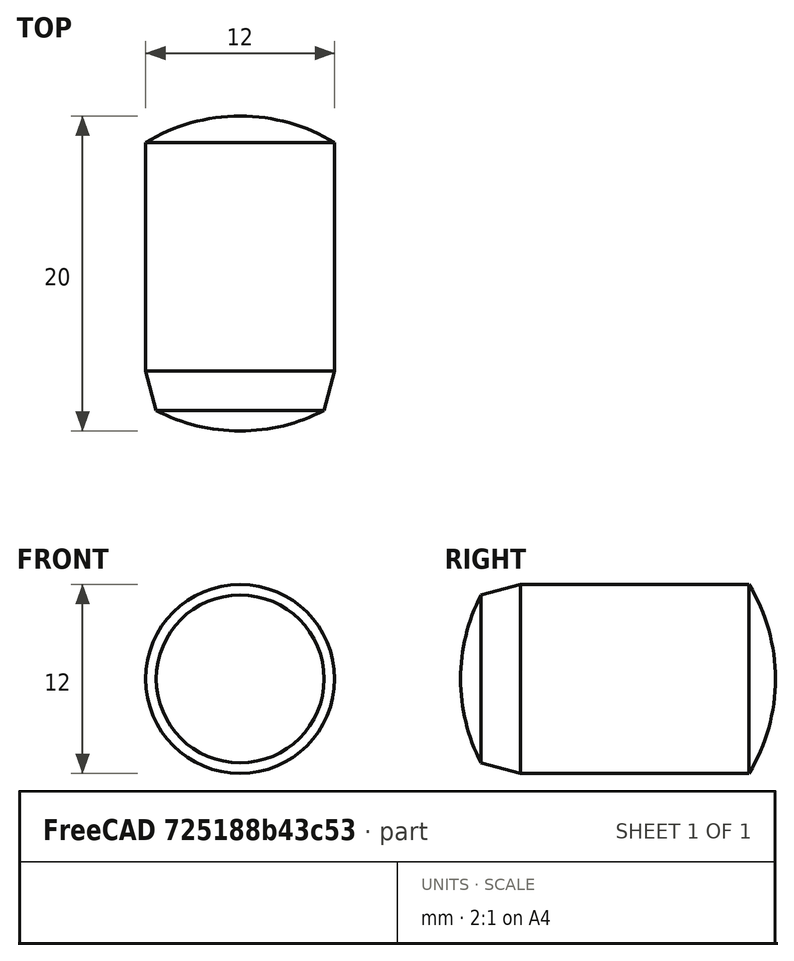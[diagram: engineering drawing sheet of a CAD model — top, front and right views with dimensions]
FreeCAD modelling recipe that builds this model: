
FCSTD DOCUMENT  (FreeCAD 0.15R4470 (Git))
Label: Zyl-Stift_DIN_6325-12x20
License: CC-BY 3.0
LicenseURL: http://creativecommons.org/licenses/by/3.0/
objects: Sketcher::SketchObject×1, PartDesign::Revolution×1
note: 3 computed .brp shape members not serialized (recipe doc carries the construction recipe); baked Part::Feature solids carry a one-line shape summary decoded from their .brp

FEATURE [Sketcher::SketchObject] Sketch
  Placement = pos=(0,0,0) rot=(0.57735,0.57735,0.57735;2.0944rad)
  sketch-geometry (5):
    g0: ArcOfCircle CenterX=10.277 CenterY=0 CenterZ=0 NormalX=0 NormalY=0 NormalZ=1 Radius=11.577 StartAngle=2.66314 EndAngle=3.14159
    g1: LineSegment StartX=0 StartY=5.33013 StartZ=0 EndX=2.5 EndY=6 EndZ=0
    g2: LineSegment StartX=2.5 StartY=6 StartZ=0 EndX=17.0239 EndY=6 EndZ=0
    g3: ArcOfCircle CenterX=7.12298 CenterY=0 CenterZ=0 NormalX=0 NormalY=0 NormalZ=1 Radius=11.577 StartAngle=0 EndAngle=0.544825
    g4: LineSegment StartX=-1.3 StartY=0 StartZ=0 EndX=18.7 EndY=0 EndZ=0
  constraints (17):
    c: PointOnObject(g0,g-1)
    c: PointOnObject(g0,g-1)
    c: PointOnObject(g0,g-2)
    c: Coincident(g0,g1)
    c: Coincident(g1,g2)
    c: Horizontal(g2)
    c: PointOnObject(g3,g-1)
    c: Coincident(g3,g2)
    c: PointOnObject(g3,g-1)
    c: Coincident(g4,g0)
    c: Coincident(g4,g3)
    c: Equal(g0,g3)
    c: Angle(g4,g1) = 0.261799
    c: DistanceX(g4) = 20
    c: DistanceY(g-1,g1) = 6
    c: DistanceX(g1) = 2.5
    c: DistanceX(g0,g0) = 1.3
FEATURE [PartDesign::Revolution] Revolution  label="Zyl-Stift DIN 6325-12x20 #"
  Angle = 360
  Axis = (0,1,0)
  Base = (0,0,0)
  Placement = pos=(0,0,0) rot=(0.57735,0.57735,0.57735;2.0944rad)
  ReferenceAxis = -> Sketch [H_Axis]
  Sketch = -> Sketch
